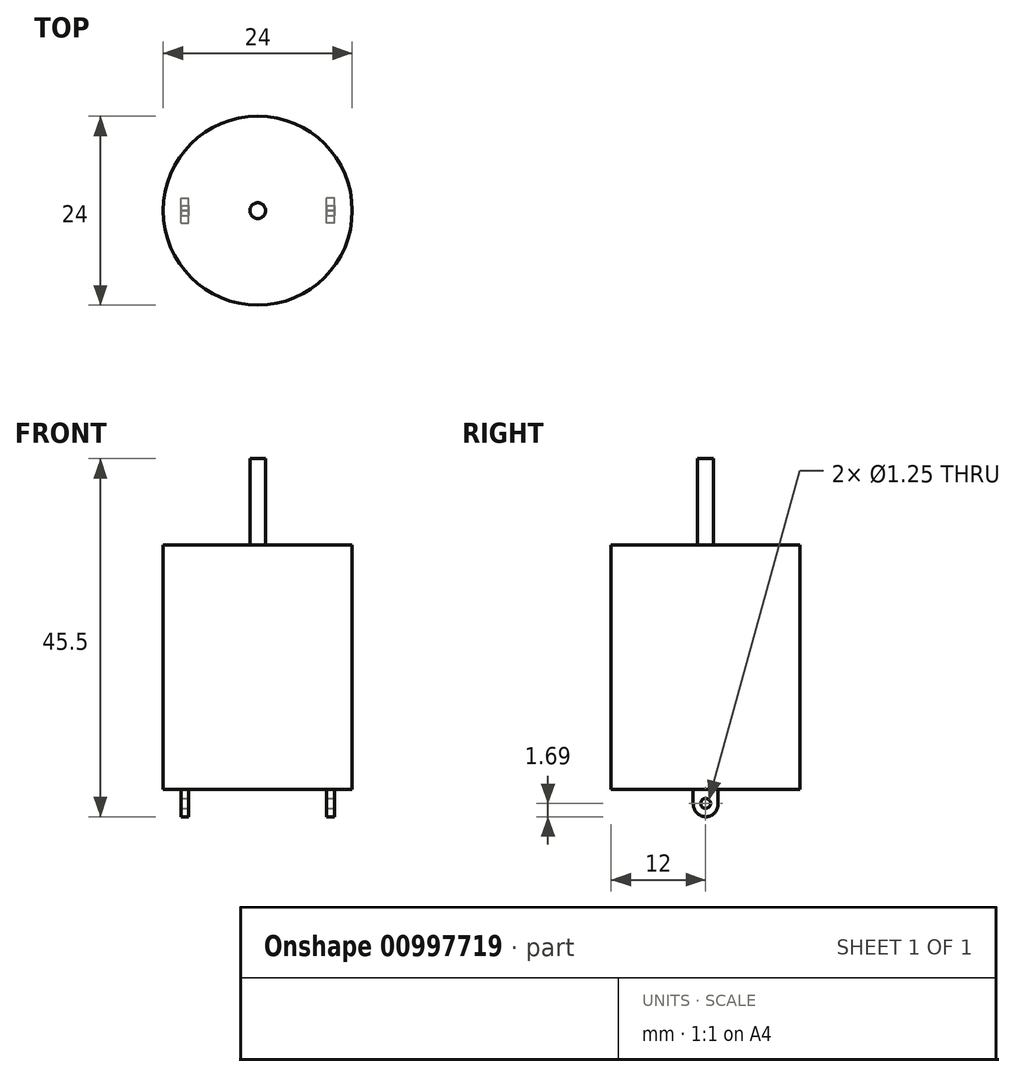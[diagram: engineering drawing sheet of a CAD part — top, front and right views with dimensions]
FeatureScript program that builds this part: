
annotation { "Feature Type Name" : "Feature", "Feature Type Description" : "" }
export const myFeature = defineFeature(function(context is Context, id is Id, definition is map)
    precondition{}
    {
        {
            var Q0;
            Q0=qCreatedBy(makeId("Top.planeOp"),FACE);
            var sketch = newSketch(context, id + "F0", { "sketchPlane" : qUnion([Q0])});
            skCircle(sketch, "E0", {"center": v(0, 0) * mm, "radius": 12 * mm});
            skSolve(sketch);
        }
        {
            var Q0;
            Q0=makeQuery(id+"F0.imprint","IMPRINT",FACE,{"disambiguationData":[TD([[makeQuery(id+"F0.imprint","IMPRINT",EDGE,{"derivedFrom":sQuery(id+"F0.wireOp",EDGE,"E0")}),1.0]])]});
            extrude(context, id + "F1", {"entities" : qUnion([Q0]), "depth" : 31 * mm, "offsetDistance" : 25 * mm});
        }
        {
            var Q0;
            Q0=makeQuery(id+"F1.opExtrude","CAP_FACE",FACE,{"disambiguationData":[OSD([sQuery(id+"F0.wireOp",EDGE,"E0")])],"isStart":false});
            var sketch = newSketch(context, id + "F2", { "sketchPlane" : qUnion([Q0])});
            skCircle(sketch, "E1", {"center": v(0, 0) * mm, "radius": 1 * mm});
            skSolve(sketch);
        }
        {
            var Q0;
            Q0=makeQuery(id+"F2.imprint","IMPRINT",FACE,{"disambiguationData":[TD([[makeQuery(id+"F2.imprint","IMPRINT",EDGE,{"derivedFrom":sQuery(id+"F2.wireOp",EDGE,"E1")}),1.0]])]});
            extrude(context, id + "F3", {"entities" : qUnion([Q0]), "operationType" : NewBodyOperationType.ADD, "depth" : 11 * mm, "offsetDistance" : 25 * mm});
        }
        {
            var Q0;
            Q0=makeQuery(id+"F1.opExtrude","CAP_FACE",FACE,{"disambiguationData":[OSD([sQuery(id+"F0.wireOp",EDGE,"E0")])],"isStart":true});
            var sketch = newSketch(context, id + "F4", { "sketchPlane" : qUnion([Q0])});
            skLineSegment(sketch, "E2", {"start": v(0, 0) * mm, "end": v(0, -3.1) * mm, "construction": true});
            skLineSegment(sketch, "E3.bottom", {"start": v(-9.73, 1.59) * mm, "end": v(-8.76, 1.59) * mm});
            skLineSegment(sketch, "E3.top", {"start": v(-9.73, -1.6) * mm, "end": v(-8.76, -1.6) * mm});
            skLineSegment(sketch, "E3.left", {"start": v(-9.73, 1.59) * mm, "end": v(-9.73, -1.6) * mm});
            skLineSegment(sketch, "E3.right", {"start": v(-8.76, 1.59) * mm, "end": v(-8.76, -1.6) * mm});
            skLineSegment(sketch, "E4.MirrorCS", {"start": v(9.73, 1.59) * mm, "end": v(9.73, -1.6) * mm});
            skLineSegment(sketch, "E5.MirrorCS", {"start": v(8.76, 1.59) * mm, "end": v(8.76, -1.6) * mm});
            skLineSegment(sketch, "E6.MirrorCS", {"start": v(9.73, 1.59) * mm, "end": v(8.76, 1.59) * mm});
            skLineSegment(sketch, "E7.MirrorCS", {"start": v(9.73, -1.6) * mm, "end": v(8.76, -1.6) * mm});
            skSolve(sketch);
        }
        {
            var Q0;
            Q0=makeQuery(id+"F4.imprint","IMPRINT",FACE,{"disambiguationData":[TD([[makeQuery(id+"F4.imprint","IMPRINT",EDGE,{"derivedFrom":sQuery(id+"F4.wireOp",EDGE,"E3.bottom")}),-1.0]])]});
            var Q1;
            Q1=makeQuery(id+"F4.imprint","IMPRINT",FACE,{"disambiguationData":[TD([[makeQuery(id+"F4.imprint","IMPRINT",EDGE,{"derivedFrom":sQuery(id+"F4.wireOp",EDGE,"E4.MirrorCS")}),-1.0]])]});
            extrude(context, id + "F5", {"entities" : qUnion([Q0, Q1]), "operationType" : NewBodyOperationType.ADD, "depth" : 3.5 * mm, "offsetDistance" : 25 * mm});
        }
        {
            var Q0;
            Q0=makeQuery(id+"F5.opExtrude","SWEPT_FACE",FACE,{"disambiguationData":[OSD([sQuery(id+"F4.wireOp",EDGE,"E4.MirrorCS")])]});
            var sketch = newSketch(context, id + "F6", { "sketchPlane" : qUnion([Q0])});
            skFitSpline(sketch, "E8", {"points": [v(-1.59, -1.75) * mm, v(0, -3.5) * mm, v(1.6, -1.75) * mm], "startDerivative": vector(0, -6.3) * mm, "endDerivative": vector(0, 6.84) * mm});
            skCircle(sketch, "E9", {"center": v(0, -1.8) * mm, "radius": 0.62 * mm});
            skSolve(sketch);
        }
        {
            var Q0;
            {var subQ0=sQuery(id+"F6.wireOp",EDGE,"E8");var subQ1=sQuery(id+"F4.wireOp",EDGE,"E4.MirrorCS");var subQ4=makeQuery(id+"F5.opExtrude","CAP_EDGE",EDGE,{"disambiguationData":[OSD([subQ1])],"isStart":false});var subQ5=makeQuery(id+"F6.imprint","INTERSECT",VERTEX,{"disambiguationData":[OD(1.0)],"derivedFrom":[subQ4,subQ0]});Q0=makeQuery(id+"F6.imprint","IMPRINT",FACE,{"disambiguationData":[TD([[makeQuery(id+"F6.imprint","IMPRINT",EDGE,{"disambiguationData":[TD([[subQ5,-1.0]])],"derivedFrom":subQ0}),-1.0]])]});}
            var Q1;
            {var subQ0=sQuery(id+"F6.wireOp",EDGE,"E8");var subQ1=sQuery(id+"F4.wireOp",EDGE,"E4.MirrorCS");var subQ4=makeQuery(id+"F5.opExtrude","CAP_EDGE",EDGE,{"disambiguationData":[OSD([subQ1])],"isStart":false});var subQ5=makeQuery(id+"F6.imprint","INTERSECT",VERTEX,{"disambiguationData":[OD(0.0)],"derivedFrom":[subQ4,subQ0]});Q1=makeQuery(id+"F6.imprint","IMPRINT",FACE,{"disambiguationData":[TD([[makeQuery(id+"F6.imprint","IMPRINT",EDGE,{"disambiguationData":[TD([[subQ5,1.0]])],"derivedFrom":subQ0}),-1.0]])]});}
            var Q2;
            Q2=makeQuery(id+"F6.imprint","IMPRINT",FACE,{"disambiguationData":[TD([[makeQuery(id+"F6.imprint","IMPRINT",EDGE,{"derivedFrom":sQuery(id+"F6.wireOp",EDGE,"E9")}),1.0]])]});
            extrude(context, id + "F7", {"entities" : qUnion([Q0, Q1, Q2]), "operationType" : NewBodyOperationType.REMOVE, "endBound" : BoundingType.THROUGH_ALL, "oppositeDirection" : true, "depth" : 25 * mm, "offsetDistance" : 25 * mm});
        }
    });
